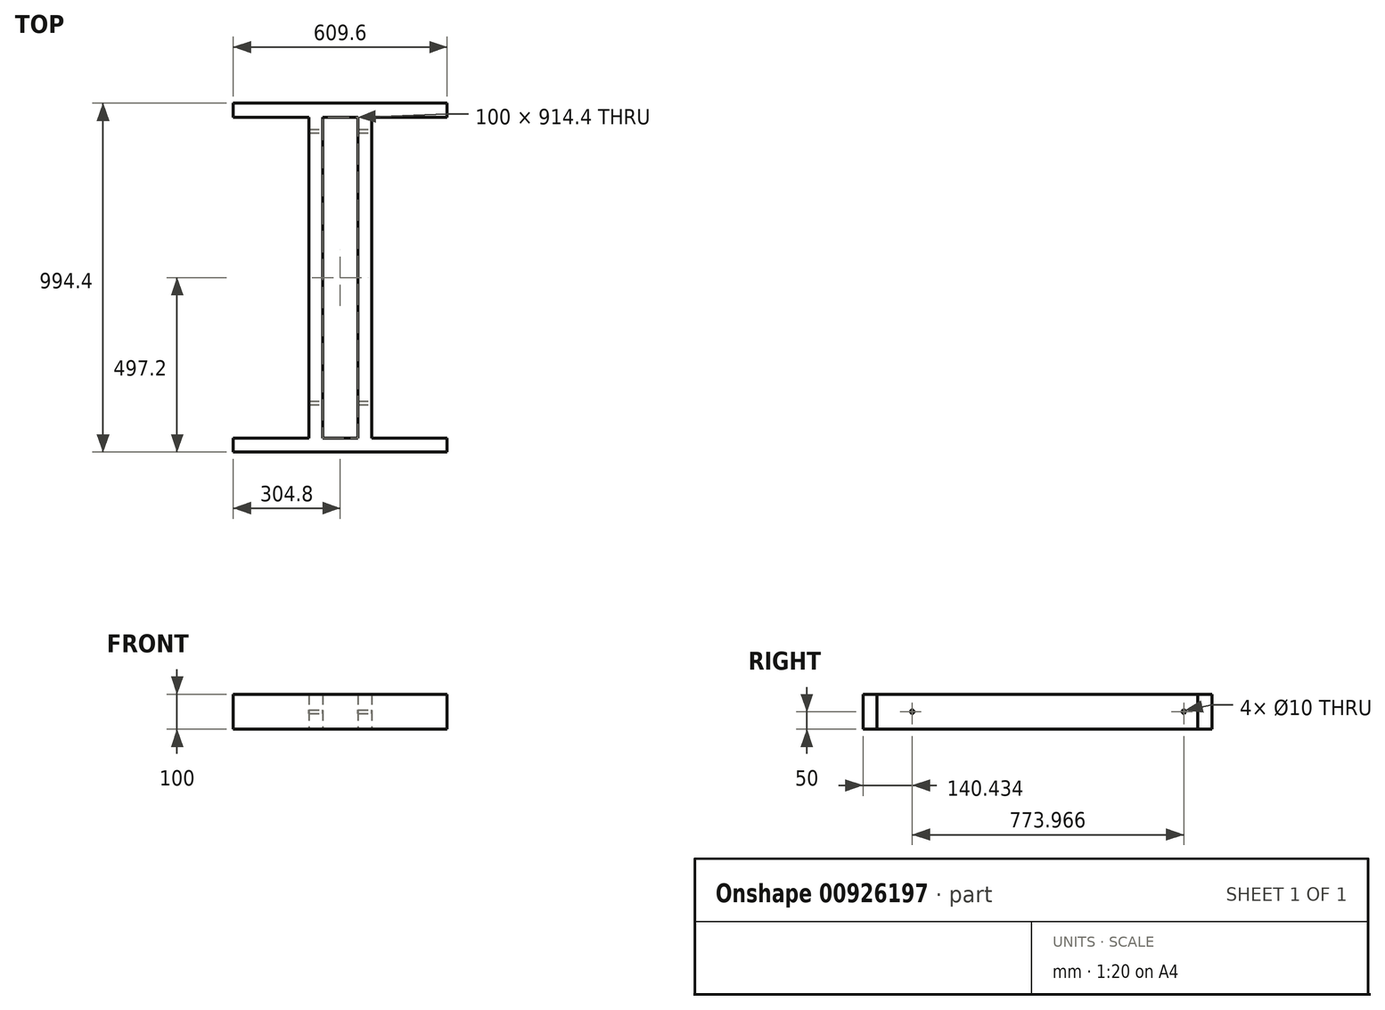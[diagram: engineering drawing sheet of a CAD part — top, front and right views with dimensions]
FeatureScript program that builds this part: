
annotation { "Feature Type Name" : "Feature", "Feature Type Description" : "" }
export const myFeature = defineFeature(function(context is Context, id is Id, definition is map)
    precondition{}
    {
        {
            var Q0;
            Q0=qCreatedBy(makeId("Top.planeOp"),FACE);
            var sketch = newSketch(context, id + "F0", { "sketchPlane" : qUnion([Q0])});
            skLineSegment(sketch, "E0.bottom", {"start": v(0, 0) * mm, "end": v(214.8, 0) * mm});
            skLineSegment(sketch, "E0.top", {"start": v(0, 40) * mm, "end": v(609.6, 40) * mm});
            skLineSegment(sketch, "E0.left", {"start": v(0, 0) * mm, "end": v(0, 40) * mm});
            skLineSegment(sketch, "E0.right", {"start": v(609.6, 0) * mm, "end": v(609.6, 40) * mm});
            skLineSegment(sketch, "E1", {"start": v(0, -457.2) * mm, "end": v(641.36, -457.2) * mm, "construction": true});
            skLineSegment(sketch, "E2.MirrorCS", {"start": v(0, -954.4) * mm, "end": v(609.6, -954.4) * mm});
            skLineSegment(sketch, "E3.MirrorCS", {"start": v(609.6, -914.4) * mm, "end": v(609.6, -954.4) * mm});
            skLineSegment(sketch, "E4.MirrorCS", {"start": v(0, -914.4) * mm, "end": v(0, -954.4) * mm});
            skLineSegment(sketch, "E5.MirrorCS", {"start": v(0, -914.4) * mm, "end": v(214.8, -914.4) * mm});
            skLineSegment(sketch, "E6", {"start": v(0, 69.5) * mm, "end": v(0, -217.18) * mm, "construction": true});
            skLineSegment(sketch, "E7", {"start": v(304.8, 0) * mm, "end": v(304.8, -914.4) * mm, "construction": true});
            skLineSegment(sketch, "E8.left", {"start": v(214.8, 0) * mm, "end": v(214.8, -914.4) * mm});
            skLineSegment(sketch, "E8.right", {"start": v(254.8, 0) * mm, "end": v(254.8, -914.4) * mm});
            skLineSegment(sketch, "E9.MirrorCS", {"start": v(354.8, 0) * mm, "end": v(354.8, -914.4) * mm});
            skLineSegment(sketch, "E10.MirrorCS", {"start": v(394.8, 0) * mm, "end": v(394.8, -914.4) * mm});
            skLineSegment(sketch, "E11.MirrorCS", {"start": v(609.6, -457.2) * mm, "end": v(-31.76, -457.2) * mm, "construction": true});
            skLineSegment(sketch, "E12.trimOffspring", {"start": v(254.8, 0) * mm, "end": v(354.8, 0) * mm});
            skLineSegment(sketch, "E13.trimOffspring", {"start": v(394.8, 0) * mm, "end": v(609.6, 0) * mm});
            skLineSegment(sketch, "E14.trimOffspring", {"start": v(254.8, -914.4) * mm, "end": v(354.8, -914.4) * mm});
            skLineSegment(sketch, "E15.trimOffspring", {"start": v(394.8, -914.4) * mm, "end": v(609.6, -914.4) * mm});
            skSolve(sketch);
        }
        {
            var Q0;
            Q0=makeQuery(id+"F0.imprint","IMPRINT",FACE,{"disambiguationData":[TD([[makeQuery(id+"F0.imprint","IMPRINT",EDGE,{"derivedFrom":sQuery(id+"F0.wireOp",EDGE,"E0.bottom")}),1.0]])]});
            extrude(context, id + "F1", {"entities" : qUnion([Q0]), "depth" : 100 * mm, "offsetDistance" : 25 * mm});
        }
        {
            var Q0;
            Q0=makeQuery(id+"F1.opExtrude","SWEPT_FACE",FACE,{"disambiguationData":[OSD([sQuery(id+"F0.wireOp",EDGE,"E10.MirrorCS")])]});
            var sketch = newSketch(context, id + "F2", { "sketchPlane" : qUnion([Q0])});
            skLineSegment(sketch, "E16", {"start": v(0, 50) * mm, "end": v(-40, 50) * mm, "construction": true});
            skLineSegment(sketch, "E17", {"start": v(-914.4, 50) * mm, "end": v(-813.97, 50) * mm, "construction": true});
            skSolve(sketch);
        }
        {
            var Q0;
            Q0=sQuery(id+"F2.wireOp",VERTEX,"E16.end");
            var Q1;
            Q1=makeQuery(id+"F1.opExtrude","SWEPT_BODY",BODY,{"disambiguationData":[OSD([sQuery(id+"F0.wireOp",EDGE,"E0.bottom"),sQuery(id+"F0.wireOp",EDGE,"E0.top"),sQuery(id+"F0.wireOp",EDGE,"E0.left"),sQuery(id+"F0.wireOp",EDGE,"E0.right"),sQuery(id+"F0.wireOp",EDGE,"E2.MirrorCS"),sQuery(id+"F0.wireOp",EDGE,"E3.MirrorCS"),sQuery(id+"F0.wireOp",EDGE,"E4.MirrorCS"),sQuery(id+"F0.wireOp",EDGE,"E5.MirrorCS"),sQuery(id+"F0.wireOp",EDGE,"E8.left"),sQuery(id+"F0.wireOp",EDGE,"E8.right"),sQuery(id+"F0.wireOp",EDGE,"E9.MirrorCS"),sQuery(id+"F0.wireOp",EDGE,"E10.MirrorCS"),sQuery(id+"F0.wireOp",EDGE,"E12.trimOffspring"),sQuery(id+"F0.wireOp",EDGE,"E13.trimOffspring"),sQuery(id+"F0.wireOp",EDGE,"E14.trimOffspring"),sQuery(id+"F0.wireOp",EDGE,"E15.trimOffspring")])]});
            hole(context, id + "F3", {"style" : HoleStyle.SIMPLE, "endStyle" : HoleEndStyle.THROUGH, "holeDiameter" : 10 * mm, "majorDiameter" : 5 * mm, "isTappedThrough" : true, "tappedDepth" : 12 * mm, "tapClearance" : 3, "locations" : qUnion([Q0]), "scope" : qUnion([Q1])});
        }
        {
            var Q0;
            Q0=sQuery(id+"F2.wireOp",VERTEX,"E17.end");
            var Q1;
            Q1=makeQuery(id+"F1.opExtrude","SWEPT_BODY",BODY,{"disambiguationData":[OSD([sQuery(id+"F0.wireOp",EDGE,"E0.bottom"),sQuery(id+"F0.wireOp",EDGE,"E0.top"),sQuery(id+"F0.wireOp",EDGE,"E0.left"),sQuery(id+"F0.wireOp",EDGE,"E0.right"),sQuery(id+"F0.wireOp",EDGE,"E2.MirrorCS"),sQuery(id+"F0.wireOp",EDGE,"E3.MirrorCS"),sQuery(id+"F0.wireOp",EDGE,"E4.MirrorCS"),sQuery(id+"F0.wireOp",EDGE,"E5.MirrorCS"),sQuery(id+"F0.wireOp",EDGE,"E8.left"),sQuery(id+"F0.wireOp",EDGE,"E8.right"),sQuery(id+"F0.wireOp",EDGE,"E9.MirrorCS"),sQuery(id+"F0.wireOp",EDGE,"E10.MirrorCS"),sQuery(id+"F0.wireOp",EDGE,"E12.trimOffspring"),sQuery(id+"F0.wireOp",EDGE,"E13.trimOffspring"),sQuery(id+"F0.wireOp",EDGE,"E14.trimOffspring"),sQuery(id+"F0.wireOp",EDGE,"E15.trimOffspring")])]});
            hole(context, id + "F4", {"style" : HoleStyle.SIMPLE, "endStyle" : HoleEndStyle.THROUGH, "holeDiameter" : 10 * mm, "majorDiameter" : 5 * mm, "isTappedThrough" : true, "tappedDepth" : 12 * mm, "tapClearance" : 3, "locations" : qUnion([Q0]), "scope" : qUnion([Q1])});
        }
    });
